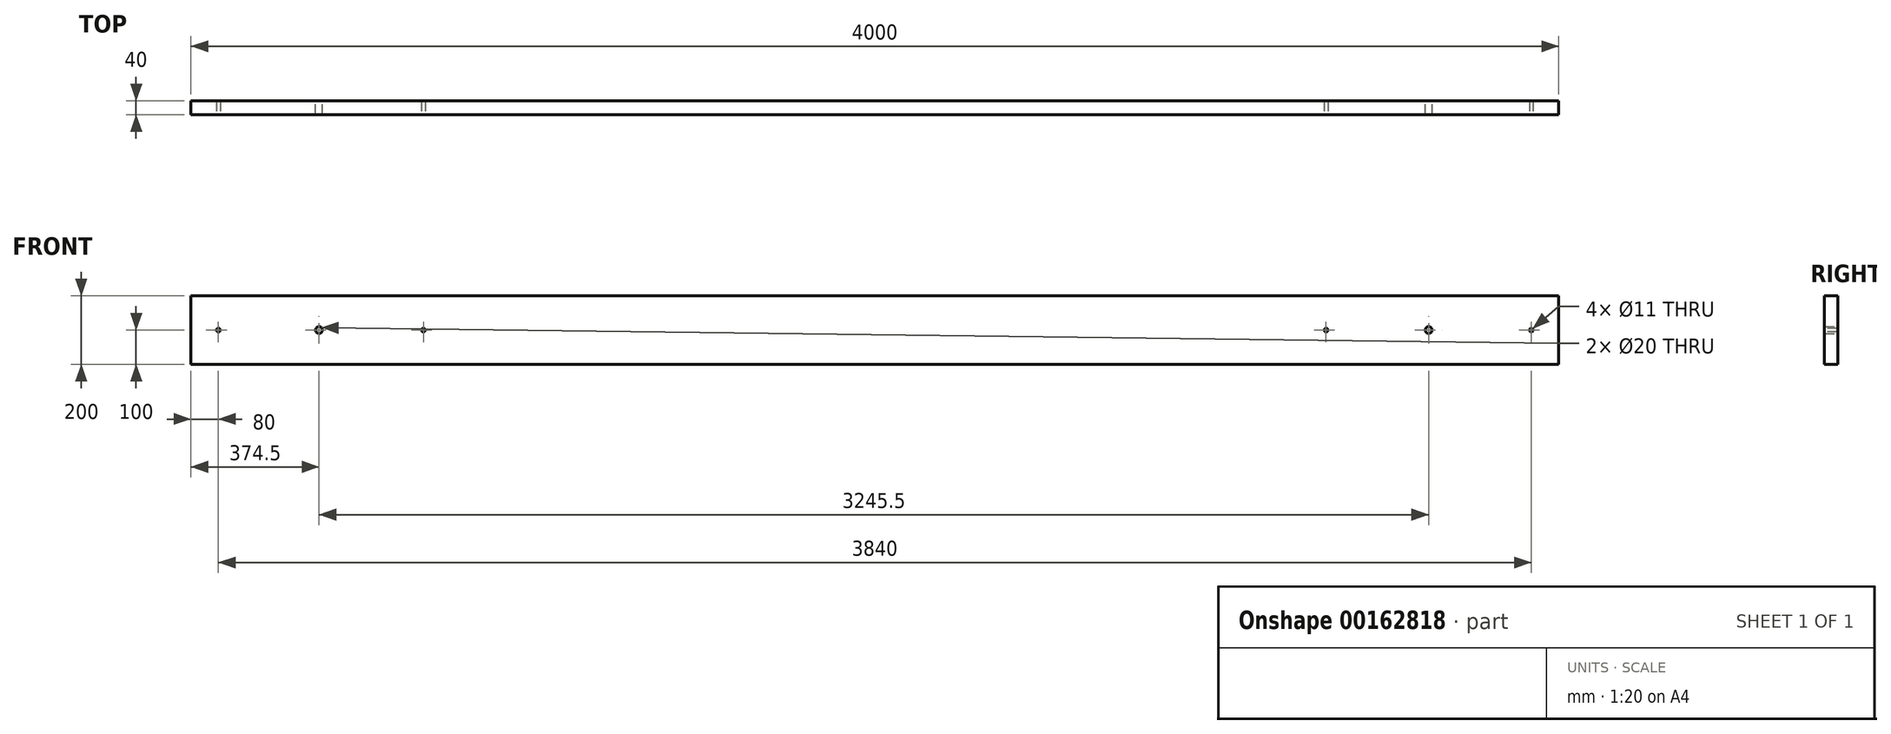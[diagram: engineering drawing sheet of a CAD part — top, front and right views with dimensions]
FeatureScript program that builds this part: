
annotation { "Feature Type Name" : "Feature", "Feature Type Description" : "" }
export const myFeature = defineFeature(function(context is Context, id is Id, definition is map)
    precondition{}
    {
        {
            var Q0;
            Q0=qCreatedBy(makeId("Right.planeOp"),FACE);
            var sketch = newSketch(context, id + "F0", { "sketchPlane" : qUnion([Q0])});
            skLineSegment(sketch, "E0.bottom", {"start": v(-20, 100) * mm, "end": v(20, 100) * mm});
            skLineSegment(sketch, "E0.top", {"start": v(-20, -100) * mm, "end": v(20, -100) * mm});
            skLineSegment(sketch, "E0.left", {"start": v(-20, 100) * mm, "end": v(-20, -100) * mm});
            skLineSegment(sketch, "E0.right", {"start": v(20, 100) * mm, "end": v(20, -100) * mm});
            skPoint(sketch, "E0.middle", {"position": v(0, 0) * mm});
            skSolve(sketch);
        }
        {
            var Q0;
            Q0=makeQuery(id+"F0.imprint","IMPRINT",FACE,{"disambiguationData":[TD([[makeQuery(id+"F0.imprint","IMPRINT",EDGE,{"derivedFrom":sQuery(id+"F0.wireOp",EDGE,"E0.bottom")}),-1.0]])]});
            extrude(context, id + "F1", {"entities" : qUnion([Q0]), "endBound" : BoundingType.SYMMETRIC, "depth" : 4000 * mm});
        }
        {
            var Q0;
            Q0=makeQuery(id+"F1.opExtrude","SWEPT_FACE",FACE,{"disambiguationData":[OSD([sQuery(id+"F0.wireOp",EDGE,"E0.left")])]});
            var sketch = newSketch(context, id + "F2", { "sketchPlane" : qUnion([Q0])});
            skPoint(sketch, "E1", {"position": v(1920, 0) * mm});
            skPoint(sketch, "E2", {"position": v(1320, 0) * mm});
            skPoint(sketch, "E3", {"position": v(-1320, 0) * mm});
            skPoint(sketch, "E4", {"position": v(-1920, 0) * mm});
            skSolve(sketch);
        }
        {
            var Q0;
            Q0=sQuery(id+"F2.wireOp",VERTEX,"E4");
            var Q1;
            Q1=sQuery(id+"F2.wireOp",VERTEX,"E3");
            var Q2;
            Q2=sQuery(id+"F2.wireOp",VERTEX,"E2");
            var Q3;
            Q3=sQuery(id+"F2.wireOp",VERTEX,"E1");
            var Q4;
            Q4=makeQuery(id+"F1.opExtrude","SWEPT_BODY",BODY,{"disambiguationData":[OSD([sQuery(id+"F0.wireOp",EDGE,"E0.bottom"),sQuery(id+"F0.wireOp",EDGE,"E0.top"),sQuery(id+"F0.wireOp",EDGE,"E0.left"),sQuery(id+"F0.wireOp",EDGE,"E0.right")])]});
            hole(context, id + "F3", {"style" : HoleStyle.SIMPLE, "endStyle" : HoleEndStyle.THROUGH, "holeDiameter" : 11 * mm, "startFromSketch" : true, "locations" : qUnion([Q0, Q1, Q2, Q3]), "scope" : qUnion([Q4]), "isTappedThrough" : true});
        }
        {
            var Q0;
            Q0=makeQuery(id+"F1.opExtrude","SWEPT_FACE",FACE,{"disambiguationData":[OSD([sQuery(id+"F0.wireOp",EDGE,"E0.right")])]});
            var sketch = newSketch(context, id + "F4", { "sketchPlane" : qUnion([Q0])});
            skPoint(sketch, "E5", {"position": v(1625.5, 0) * mm});
            skPoint(sketch, "E6", {"position": v(-1620, 0) * mm});
            skCircle(sketch, "E7.0", {"center": v(-1920, 0) * mm, "radius": 5.5 * mm});
            skSolve(sketch);
        }
        {
            var Q0;
            Q0=sQuery(id+"F4.wireOp",VERTEX,"E5");
            var Q1;
            Q1=sQuery(id+"F4.wireOp",VERTEX,"E6");
            var Q2;
            Q2=makeQuery(id+"F1.opExtrude","SWEPT_BODY",BODY,{"disambiguationData":[OSD([sQuery(id+"F0.wireOp",EDGE,"E0.bottom"),sQuery(id+"F0.wireOp",EDGE,"E0.top"),sQuery(id+"F0.wireOp",EDGE,"E0.left"),sQuery(id+"F0.wireOp",EDGE,"E0.right")])]});
            hole(context, id + "F5", {"style" : HoleStyle.SIMPLE, "endStyle" : HoleEndStyle.THROUGH, "holeDiameter" : 20 * mm, "startFromSketch" : true, "locations" : qUnion([Q0, Q1]), "scope" : qUnion([Q2]), "isTappedThrough" : true});
        }
    });
